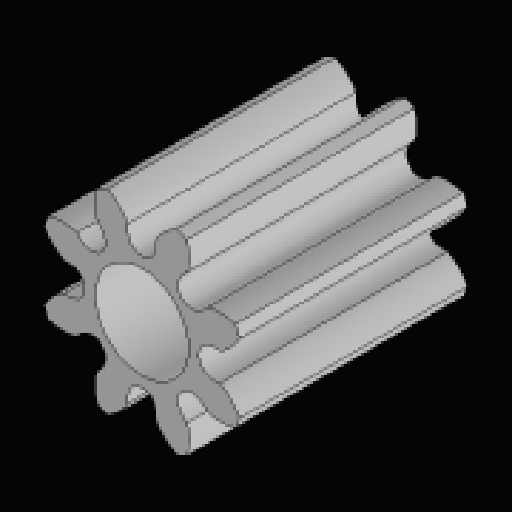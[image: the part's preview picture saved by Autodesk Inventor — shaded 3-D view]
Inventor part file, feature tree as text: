
AUTODESK INVENTOR PART (.ipt)
format: ipt  version: 2023.2 (Build 272271030, 271C)  size: 662,016 bytes
history: native  units: mm
features: sketch x2, extrude x2, pattern_circular x1, hole x1, chamfer x1
ambient origin geometry x8: Origin, YZ Plane, XZ Plane, XY Plane, X Axis, Y Axis, Z Axis, Center Point
bodies: Solid1 (feature_tree)
feature tree (7):
  sketch  "Sketch1"  dims[d0=11.0mm d1=0.0mm d2=0.0mm d3=0.0mm]
  extrude  "Extrusion1"  TaperAngle=0.0deg  [1 undecoded]
  extrude  "Extrusion2"  Depth=0.5mm TaperAngle=45.0deg
  pattern_circular  "Circular Pattern1"  [2 undecoded]
  hole  "Hole1"  [1 undecoded]
  chamfer  "Chamfer1"  [1 undecoded]
  sketch  "Sketch2"  dims[d4=80.0mm d5=360.0deg d7=2.5mm d8=6.0mm d9=4.5mm d10=7.5mm d11=90.0deg d12=8.0mm d13=20.594885mm d14=0.5mm d15=2.0mm d16=45.0deg]
note: 5 required parameter values undecoded (feature->parameter linkage not recoverable at this tier; creation-order binding heuristic only, values carry confidence <= 0.55)
